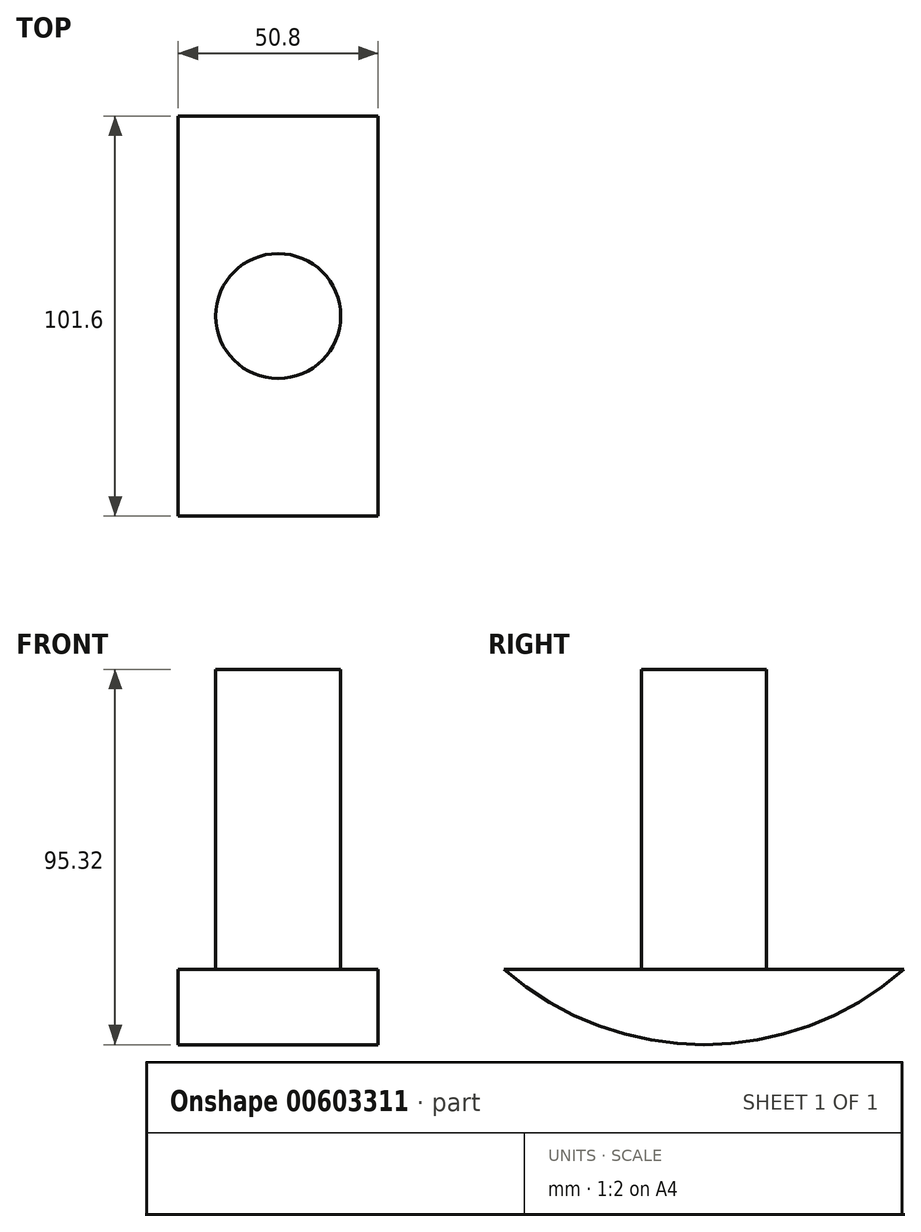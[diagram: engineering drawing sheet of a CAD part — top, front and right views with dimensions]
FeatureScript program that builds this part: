
annotation { "Feature Type Name" : "Feature", "Feature Type Description" : "" }
export const myFeature = defineFeature(function(context is Context, id is Id, definition is map)
    precondition{}
    {
        {
            var Q0;
            Q0=qCreatedBy(makeId("Top.planeOp"),FACE);
            var sketch = newSketch(context, id + "F0", { "sketchPlane" : qUnion([Q0])});
            skCircle(sketch, "E0", {"center": v(0, 0) * mm, "radius": 15.88 * mm});
            skSolve(sketch);
        }
        {
            var Q0;
            Q0 = qSketchRegion(id + "F0", true);
            extrude(context, id + "F1", {"entities" : qUnion([Q0]), "depth" : 76.2 * mm, "offsetDistance" : 25.4 * mm});
        }
        {
            var Q0;
            Q0=qCreatedBy(makeId("Right.planeOp"),FACE);
            var sketch = newSketch(context, id + "F2", { "sketchPlane" : qUnion([Q0])});
            skLineSegment(sketch, "E1", {"start": v(0, 0) * mm, "end": v(50.8, 0) * mm});
            skLineSegment(sketch, "E2", {"start": v(0, 0) * mm, "end": v(-50.8, 0) * mm});
            skArc(sketch, "E3", {"start": v(-50.8, 0) * mm, "mid": v(0, -19.12) * mm, "end": v(50.8, 0) * mm});
            skSolve(sketch);
        }
        {
            var Q0;
            Q0 = qSketchRegion(id + "F2", true);
            extrude(context, id + "F3", {"entities" : qUnion([Q0]), "operationType" : NewBodyOperationType.ADD, "depth" : 25.4 * mm, "offsetDistance" : 25.4 * mm});
        }
        {
            var Q0;
            Q0 = qSketchRegion(id + "F2", true);
            extrude(context, id + "F4", {"entities" : qUnion([Q0]), "operationType" : NewBodyOperationType.ADD, "oppositeDirection" : true, "depth" : 25.4 * mm, "offsetDistance" : 25.4 * mm});
        }
    });
